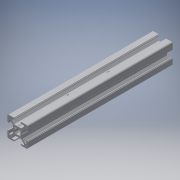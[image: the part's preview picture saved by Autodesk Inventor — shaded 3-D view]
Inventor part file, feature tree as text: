
AUTODESK INVENTOR PART (.ipt)
format: ipt  version: 2016 (Build 200138000, 138)  size: 412,160 bytes
history: native  units: in
note: dims shown in document units (in); Inventor stores cm internally (conversion verified against a paired STEP export)
features: other x3, sketch x2, extrude x1, hole x1, mirror x1
ambient origin geometry x8: Origin, YZ Plane, XZ Plane, XY Plane, X Axis, Y Axis, Z Axis, Center Point
bodies: Solid1 (feature_tree)
feature tree (8):
  other  "Blocks"
  extrude  "Extrusion1"  Depth=2.0in
  hole  "Hole1"  [1 undecoded]
  mirror  "Mirror1"
  sketch  "Sketch1"  dims[d1=0.0in d5=2.0in]
  other  "20x20"
  sketch  "Sketch3"  dims[d6=0.187in d7=0.75in d8=0.375in d9=0.25in d10=0.5635in d11=1.0in d12=0.8108in d13=1.0in d14=1.0in]
  other  "20x20:1"
note: 1 required parameter value undecoded (feature->parameter linkage not recoverable at this tier; creation-order binding heuristic only, values carry confidence <= 0.55)
